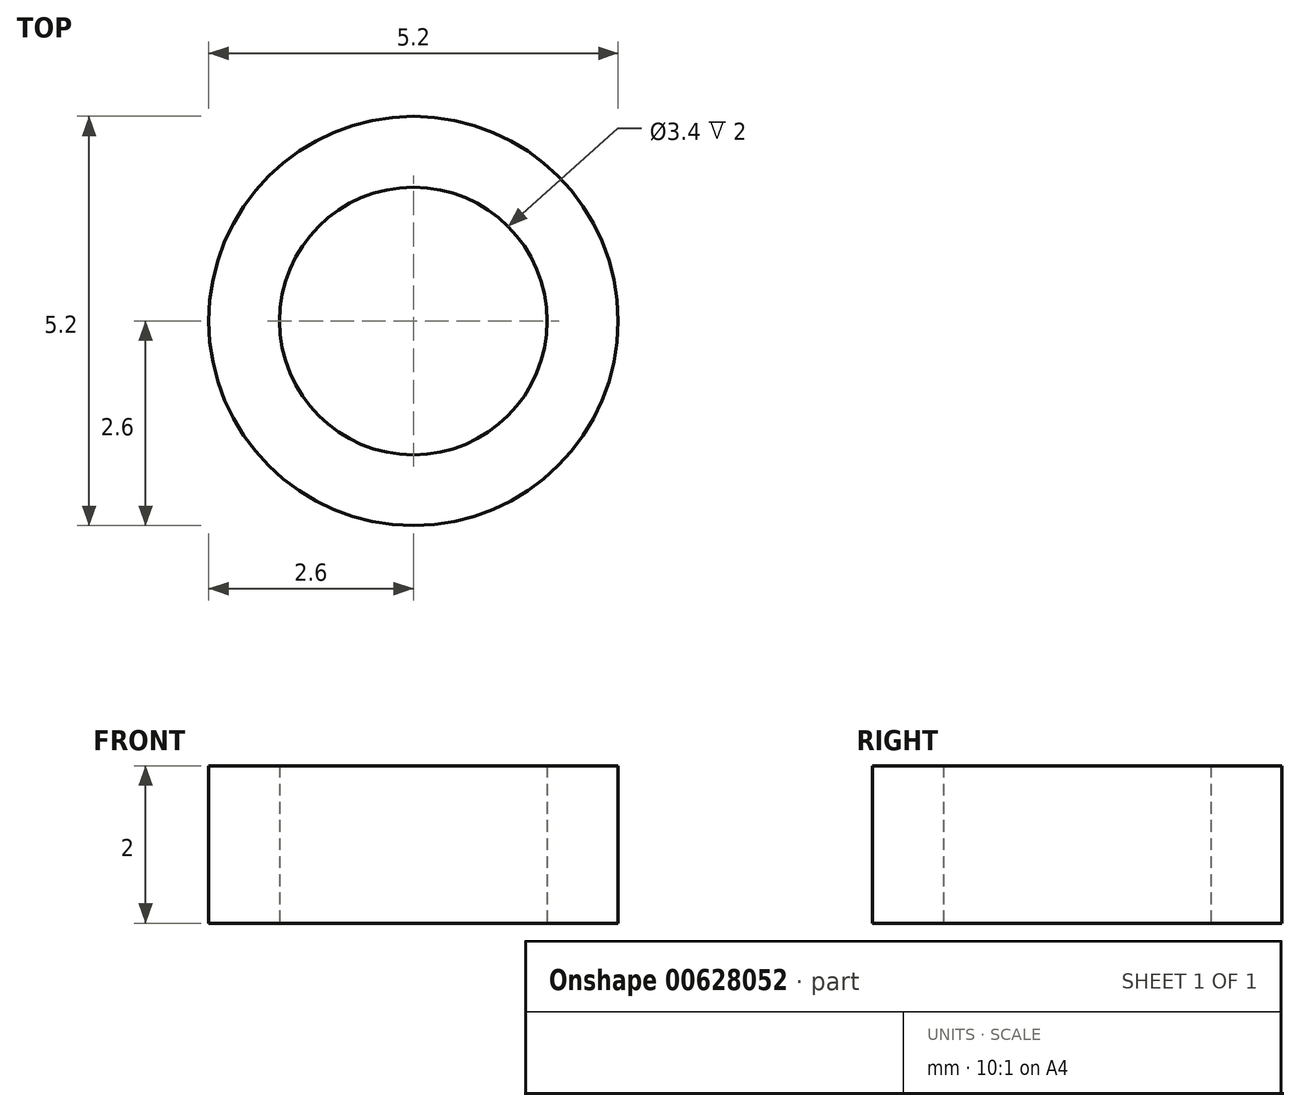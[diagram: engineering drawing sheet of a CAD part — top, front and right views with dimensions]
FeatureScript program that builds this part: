
annotation { "Feature Type Name" : "Feature", "Feature Type Description" : "" }
export const myFeature = defineFeature(function(context is Context, id is Id, definition is map)
    precondition{}
    {
        {
            var Q0;
            Q0=qCreatedBy(makeId("Top.planeOp"),FACE);
            var sketch = newSketch(context, id + "F0", { "sketchPlane" : qUnion([Q0])});
            skCircle(sketch, "E0", {"center": v(0, 0) * mm, "radius": 1.7 * mm});
            skCircle(sketch, "E1", {"center": v(0, 0) * mm, "radius": 2.6 * mm});
            skSolve(sketch);
        }
        {
            var Q0;
            Q0=makeQuery(id+"F0.imprint","IMPRINT",FACE,{"disambiguationData":[TD([[makeQuery(id+"F0.imprint","IMPRINT",EDGE,{"derivedFrom":sQuery(id+"F0.wireOp",EDGE,"E0")}),-1.0]])]});
            extrude(context, id + "F1", {"entities" : qUnion([Q0]), "depth" : 2 * mm, "offsetDistance" : 25 * mm});
        }
    });
